# Revit family: 3031810 Lighting Fixture_Sylvania_Syl-Lighter II_Ceiling Recessed
name_source: partatom
category: Lighting Fixtures
revit_build: Autodesk Revit 2017 (Build: 20190507_1515(x64)
units: mm (PartAtom-declared; Revit-internal decimal feet)

## family parameters
Cut with Voids When Loaded = No
Host = Face
Light Source = Yes
OmniClass Number = 23.80.70.11.17
OmniClass Title = Specialized Lighting by Location or Use
Part Type = Normal
Room Calculation Point = No
Round Connector Dimension = Use Diameter
Shared = No

## types (1)
- Syl-Lighter LED II 195 RO 15W WW 1-10V
    Accessory Diameter = 195 mm  [stored 0.639764 ft]
    Accessory Material = Aluminum_Sylvania_Syl-Lighter LED II_White_RAL 9003
    Accessory Radius = 97.5 mm  [stored 0.319882 ft]
    Apparent Load = 15 VA
    Assembly Code = D5020200
    Beam Angle = 74.00°
    Body Material = Metal_Sylvania_Syl-Lighter LED II_Silver
    Catalog Number = 3031810 Syl-Lighter LED II 195 RO 15W WW 1-10V
    Color Filter = 16777215
    Cutout Diameter = 175 mm  [stored 0.574147 ft]
    Default Elevation = 0 mm  [stored 0 ft]
    Description = Syl-Lighter LED II is available in 4 different round body sizes: 165mm, 195mm, 220mm & 240mm Syl-Lighter LED II 165 12W delivers a 1,134 lumen output (4,000K) - perfect for 1x26W CFL replacement Syl-Lighter LED II 195 15W delivers a 1,480 lumen output (4,000K) - perfect for 1x32W/2x18W CFL replacement Syl-Lighter LED II 220 21W delivers a 1,989 lumen output (4,000K) - perfect for 1x42W CFL replacement Syl-Lighter LED II 240 25W delivers a 2,289 lumen output (4,000K)- perfect for 2x26W CFL replacement High efficacy up to 99lm/W (Syl-Lighter LED II 195 4,000K) IP44 rating allows for installation in applicable wet zone areas Choice of 3,000K (warm white) or 4,000K (neutral white) Shallow recess depth of <65mm Can replace existing large CFL downlights using a 225mm ceiling cut out (Syl-Lighter LED II 240) Energy efficient electronic gear including analogue 1-10V and DALI dimmable options IK07 polycarbonate diffuser allows for a wider light distribution than a reflector downlight, allowing for increased spacings between luminaires 3 hour emergency pack available (to be ordered in addition to the luminaire) Ideal for applications such as corridors, public WCs and back of house areas Quick and easy to install Loop in-Loop out facility with red push fit terminal block for quick wiring White bezel (RAL 9003) Energy Class: A++, A+, A Long lifetime: 50,000 hours life at L70 (L80: 30,000 hours, L90: 15,000 hours)
    Diameter = 175 mm  [stored 0.574147 ft]
    Diffuser Diameter = 155 mm
    Diffuser Material = Polycarbonate_Sylvania_Syl-Lighter LED II_Opal
    Diffuser Radius = 77.5 mm
    Dimmable = DALI
    Dimming Lamp Color Temperature Shift = <None>
    Drive Current = 300mA
    Electrical Protection = CLASS II
    Emit Shape Visible in Rendering = No
    Emit from Circle Diameter = 155 mm
    Energy Class = A++, A+, A
    Glow Wire Test = 650 °C
    Height = 55 mm  [stored 0.180446 ft]
    IK Rating = IK07
    IP Rating = IP44
    Inner Diameter = 171 mm  [stored 0.561024 ft]
    Lamp = LED
    Lamp Comments = Integrated LED
    Life = 50 000h
    Manufacturer = Feilo Sylvania
    Model = Syl-Lighter LED II 195 RO 15W WW 1-10V
    Photometric Web File = 3031810_Syl-LighterLEDII195RO15WWW1-10V-187577.ies
    Product Family = SYL-LIGHTER LED II
    Product Page URL = http://www.sylvania-lighting.com
    Recessed Depth = 55 mm  [stored 0.180446 ft]
    Ta Rating = -10°C to +40°C
    Tilt Angle = -90.00°
    URL = http://www.sylvania-lighting.com
    Voltage = 240 V
    Voltage Comments = UNV (Universal Voltage; 220-240 Volt)
    Weight = 0.45 kg

note: [stored X ft] marks values corroborated as IEEE doubles in the binary element streams (Revit-internal decimal feet)

## geometry (parser evidence)
native form markers: Blend x4, Sweep x1
no freeform markers — native parametric forms only
